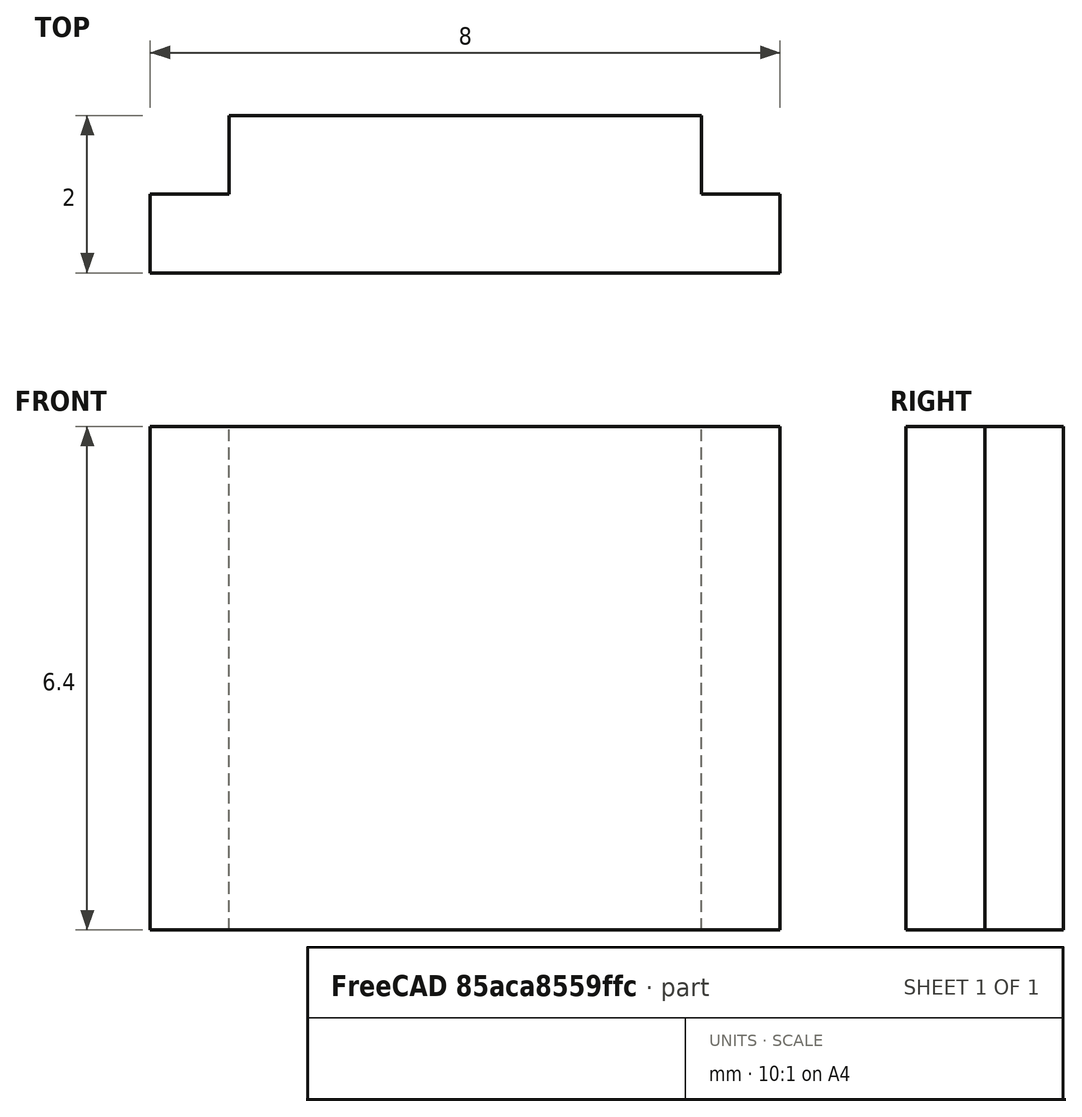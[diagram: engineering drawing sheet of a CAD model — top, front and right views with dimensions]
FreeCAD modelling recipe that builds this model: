
FCSTD DOCUMENT  (FreeCAD 0.19R24291 (Git))
Label: diffusor
License: All rights reserved
LicenseURL: http://en.wikipedia.org/wiki/All_rights_reserved
objects: Sketcher::SketchObject×1, PartDesign::Pad×1, PartDesign::Body×1
note: 4 computed .brp shape members not serialized (recipe doc carries the construction recipe); baked Part::Feature solids carry a one-line shape summary decoded from their .brp

FEATURE [Sketcher::SketchObject] Sketch
  FullyConstrained = true
  MapMode = 5
  Support = -> [XY_Plane]
  sketch-geometry (8):
    g0: LineSegment StartX=0 StartY=0 StartZ=0 EndX=6 EndY=0 EndZ=0
    g1: LineSegment StartX=6 StartY=0 StartZ=0 EndX=6 EndY=-1 EndZ=0
    g2: LineSegment StartX=6 StartY=-1 StartZ=0 EndX=7 EndY=-1 EndZ=0
    g3: LineSegment StartX=7 StartY=-1 StartZ=0 EndX=7 EndY=-2 EndZ=0
    g4: LineSegment StartX=7 StartY=-2 StartZ=0 EndX=-1 EndY=-2 EndZ=0
    g5: LineSegment StartX=-1 StartY=-2 StartZ=0 EndX=-1 EndY=-1 EndZ=0
    g6: LineSegment StartX=-1 StartY=-1 StartZ=0 EndX=0 EndY=-1 EndZ=0
    g7: LineSegment StartX=0 StartY=-1 StartZ=0 EndX=0 EndY=0 EndZ=0
  constraints (23):
    c: Coincident(g-1,g0)
    c: PointOnObject(g0,g-1)
    c: Coincident(g0,g1)
    c: Vertical(g1)
    c: Coincident(g1,g2)
    c: Horizontal(g2)
    c: Coincident(g2,g3)
    c: Vertical(g3)
    c: Coincident(g3,g4)
    c: Horizontal(g4)
    c: Coincident(g4,g5)
    c: Vertical(g5)
    c: Coincident(g5,g6)
    c: PointOnObject(g6,g-2)
    c: Horizontal(g6)
    c: Coincident(g6,g7)
    c: Coincident(g7,g0)
    c: DistanceX(g0,g0) = 6
    c: DistanceY(g1,g1) = 1
    c: DistanceY(g7,g7) = 1
    c: DistanceY(g5,g5) = 1
    c: DistanceX(g6,g6) = 1
    c: DistanceX(g2,g2) = 1
FEATURE [PartDesign::Pad] Pad
  Direction = (1,1,1)
  Length = 6.4
  Length2 = 100
  Profile = -> Sketch
  Type = 0
FEATURE [PartDesign::Body] Body
  Group = -> [Sketch,Pad]
  Origin = -> Origin
  Tip = -> Pad
